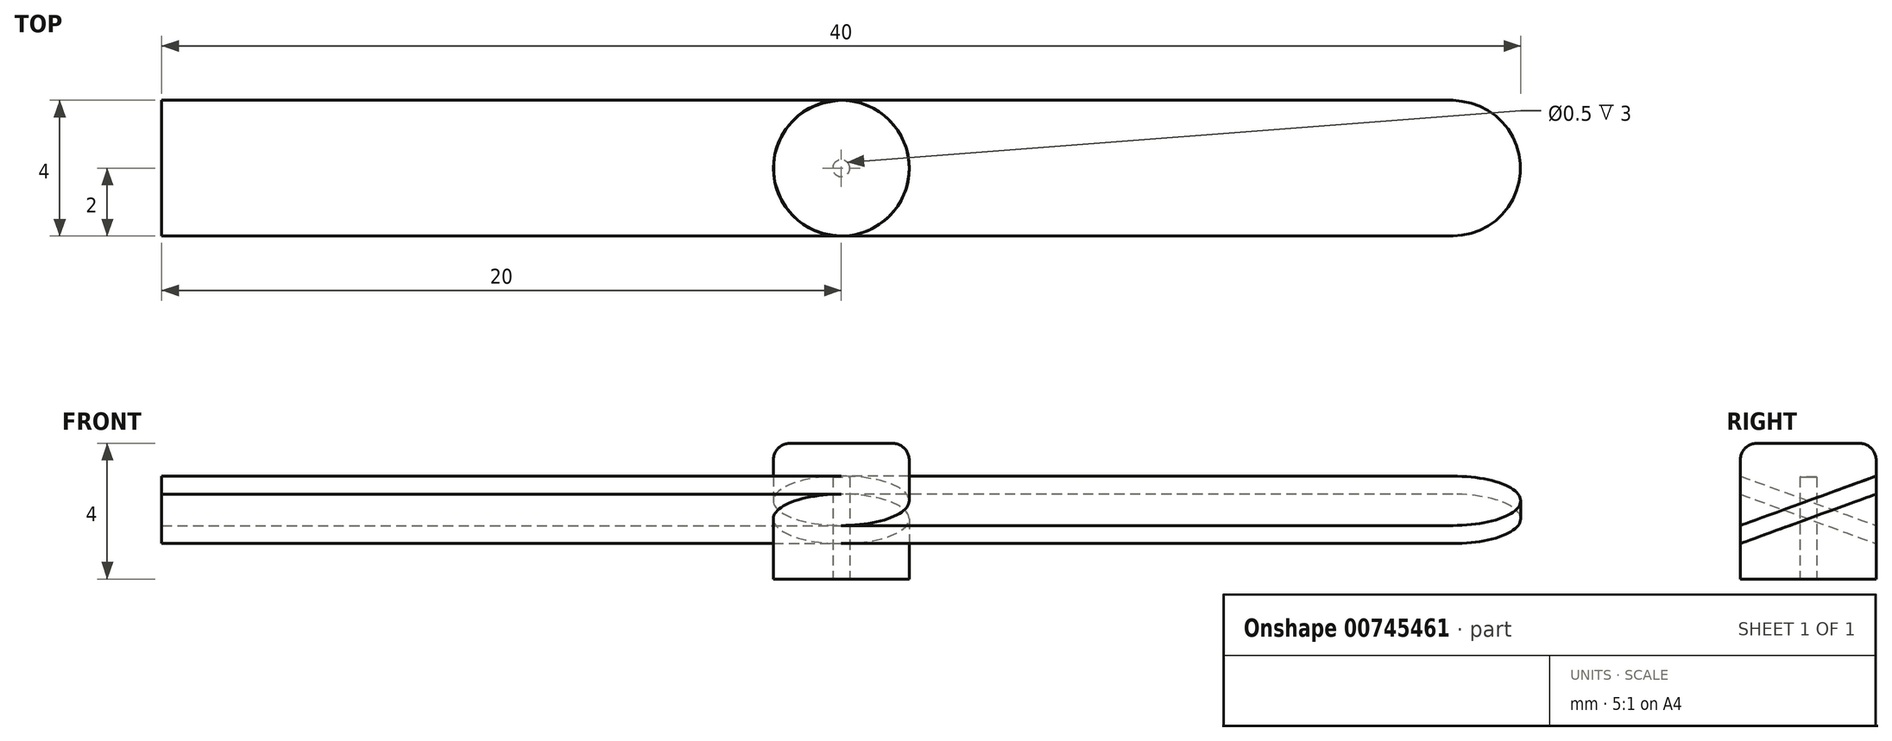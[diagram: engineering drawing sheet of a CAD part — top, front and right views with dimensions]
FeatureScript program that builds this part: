
annotation { "Feature Type Name" : "Feature", "Feature Type Description" : "" }
export const myFeature = defineFeature(function(context is Context, id is Id, definition is map)
    precondition{}
    {
        {
            var Q0;
            Q0=qCreatedBy(makeId("Top.planeOp"),FACE);
            var sketch = newSketch(context, id + "F0", { "sketchPlane" : qUnion([Q0])});
            skCircle(sketch, "E0", {"center": v(0, 0) * mm, "radius": 2 * mm});
            skSolve(sketch);
        }
        {
            var Q0;
            Q0=makeQuery(id+"F0.imprint","IMPRINT",FACE,{"disambiguationData":[TD([[makeQuery(id+"F0.imprint","IMPRINT",EDGE,{"derivedFrom":sQuery(id+"F0.wireOp",EDGE,"E0")}),1.0]])]});
            extrude(context, id + "F1", {"entities" : qUnion([Q0]), "depth" : 4 * mm, "offsetDistance" : 25 * mm});
        }
        {
            var Q0;
            Q0=qCreatedBy(makeId("Right.planeOp"),FACE);
            var sketch = newSketch(context, id + "F2", { "sketchPlane" : qUnion([Q0])});
            skLineSegment(sketch, "E1", {"start": v(-2, 0.3) * mm, "end": v(-2, 2.86) * mm, "construction": true});
            skLineSegment(sketch, "E2", {"start": v(2, 4) * mm, "end": v(2, 0) * mm, "construction": true});
            skLineSegment(sketch, "E3", {"start": v(-2, 1.58) * mm, "end": v(2, 3.03) * mm});
            skLineSegment(sketch, "E4", {"start": v(-2, 1.04) * mm, "end": v(2, 2.5) * mm});
            skLineSegment(sketch, "E5", {"start": v(-2, 1.58) * mm, "end": v(-2, 1.04) * mm});
            skLineSegment(sketch, "E6", {"start": v(2, 3.03) * mm, "end": v(2, 2.5) * mm});
            skSolve(sketch);
        }
        {
            var Q0;
            Q0 = qSketchRegion(id + "F2", true);
            extrude(context, id + "F3", {"entities" : qUnion([Q0]), "operationType" : NewBodyOperationType.ADD, "depth" : 20 * mm, "offsetDistance" : 25 * mm});
        }
        {
            var Q0;
            Q0=qCreatedBy(makeId("Right.planeOp"),FACE);
            var sketch = newSketch(context, id + "F4", { "sketchPlane" : qUnion([Q0])});
            skLineSegment(sketch, "E7", {"start": v(2, 3.15) * mm, "end": v(2, 0) * mm});
            skLineSegment(sketch, "E8", {"start": v(-2, 0) * mm, "end": v(-2, 4) * mm});
            skLineSegment(sketch, "E9", {"start": v(2, 4) * mm, "end": v(2, 0) * mm, "construction": true});
            skLineSegment(sketch, "E10", {"start": v(-2, 0) * mm, "end": v(-2, 4) * mm, "construction": true});
            skLineSegment(sketch, "E11", {"start": v(-2, 3.03) * mm, "end": v(2, 1.58) * mm});
            skLineSegment(sketch, "E12", {"start": v(-2, 2.5) * mm, "end": v(2, 1.04) * mm});
            skLineSegment(sketch, "E13", {"start": v(2, 1.04) * mm, "end": v(2, 1.58) * mm});
            skLineSegment(sketch, "E14", {"start": v(-2, 2.5) * mm, "end": v(-2, 3.03) * mm});
            skSolve(sketch);
        }
        {
            var Q0;
            Q0 = qSketchRegion(id + "F4", true);
            extrude(context, id + "F5", {"entities" : qUnion([Q0]), "operationType" : NewBodyOperationType.ADD, "oppositeDirection" : true, "depth" : 20 * mm, "offsetDistance" : 25 * mm});
        }
        {
            var Q0;
            Q0=makeQuery(id+"F5.opExtrude","CAP_EDGE",EDGE,{"disambiguationData":[OSD([sQuery(id+"F4.wireOp",EDGE,"E13")])],"isStart":false});
            var Q1;
            Q1=makeQuery(id+"F5.opExtrude","CAP_EDGE",EDGE,{"disambiguationData":[OSD([sQuery(id+"F4.wireOp",EDGE,"E14")])],"isStart":false});
            var Q2;
            Q2=makeQuery(id+"F3.opExtrude","CAP_EDGE",EDGE,{"disambiguationData":[OSD([sQuery(id+"F2.wireOp",EDGE,"E5")])],"isStart":false});
            var Q3;
            Q3=makeQuery(id+"F3.opExtrude","CAP_EDGE",EDGE,{"disambiguationData":[OSD([sQuery(id+"F2.wireOp",EDGE,"E6")])],"isStart":false});
            fillet(context, id + "F6", {"entities" : qUnion([Q0, Q1, Q2, Q3]), "radius" : 2 * mm, "tangentPropagation" : true, "allowEdgeOverflow" : false});
        }
        {
            var Q0;
            Q0=makeQuery(id+"F1.opExtrude","CAP_EDGE",EDGE,{"disambiguationData":[OSD([sQuery(id+"F0.wireOp",EDGE,"E0")])],"isStart":false});
            fillet(context, id + "F7", {"entities" : qUnion([Q0]), "radius" : 0.5 * mm, "tangentPropagation" : true, "allowEdgeOverflow" : false});
        }
        {
            var Q0;
            Q0=makeQuery(id+"F1.opExtrude","CAP_FACE",FACE,{"disambiguationData":[OSD([sQuery(id+"F0.wireOp",EDGE,"E0")])],"isStart":true});
            var sketch = newSketch(context, id + "F8", { "sketchPlane" : qUnion([Q0])});
            skCircle(sketch, "E15", {"center": v(0, 0) * mm, "radius": 0.25 * mm});
            skSolve(sketch);
        }
        {
            var Q0;
            Q0=makeQuery(id+"F8.imprint","IMPRINT",FACE,{"disambiguationData":[TD([[makeQuery(id+"F8.imprint","IMPRINT",EDGE,{"derivedFrom":sQuery(id+"F8.wireOp",EDGE,"E15")}),1.0]])]});
            extrude(context, id + "F9", {"entities" : qUnion([Q0]), "operationType" : NewBodyOperationType.REMOVE, "oppositeDirection" : true, "depth" : 3 * mm, "offsetDistance" : 25 * mm});
        }
    });
